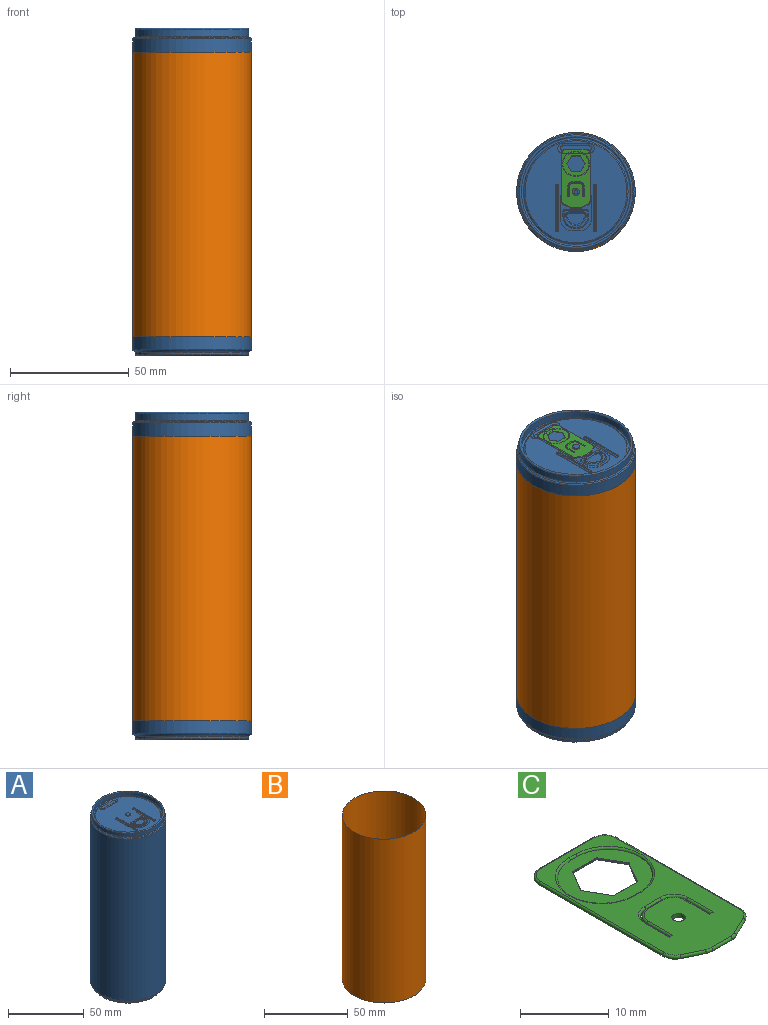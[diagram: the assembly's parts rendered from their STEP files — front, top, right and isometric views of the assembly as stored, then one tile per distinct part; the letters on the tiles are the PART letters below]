
ASSEMBLY  parts=3 mates=2
PART A: 76 faces, bbox 54.1x54.1x138 mm
  f0: plane 43x43mm, normal (0,0,1), area 1250.3mm2, adj f1,f7,f8,f9,f14,f18,f19,f20
  f1: plane 1x0.01mm, normal (0,-1,0), area 0mm2, adj f0,f9,f18
  f2: cylinder r=25mm len=131mm, axis (0,0,-1), area 20577.4mm2, adj f60,f66
  f3: cylinder r=24mm len=48mm, axis (0,0,1), area 150.8mm2, adj f67,f68
  f4: plane 43x43mm, normal (0,0,-1), area 1452.2mm2, adj f75
  f5: cylinder r=23mm len=46mm, axis (0,0,-1), area 433.5mm2, adj f59,f62
  f6: cylinder r=24mm len=48mm, axis (0,0,-1), area 452.4mm2, adj f61,f62
  f7: plane 3x1mm, normal (0,1,0), area 3mm2, adj f0,f10,f25,f26
  f8: plane 10.02x1.02mm, normal (-1,0,0), area 10mm2, adj f0,f10,f19,f25
  f9: plane 10x1mm, normal (1,0,0), area 10mm2, adj f0,f1,f10,f26
  f10: plane 41x41mm, normal (0,0,-1), area 1319.8mm2, adj f7,f8,f9,f18,f19,f20,f23,f24
  f11: plane 48x48mm, normal (0,0,1), area 1809.6mm2, adj f69
  f12: cylinder r=24.5mm len=129mm, axis (0,0,-1), area 19858mm2, adj f65,f69
  f13: plane 48x48mm, normal (0,0,-1), area 357.4mm2, adj f63,f65
  f14: cylinder r=0.75mm len=1.5mm, axis (0,0,-1), area 2.4mm2, adj f0,f17
  f15: cylinder r=1.5mm len=3mm, axis (0,0,-1), area 4.7mm2, adj f16,f17
  f16: plane 3x3mm, normal (0,0,1), area 7.1mm2, adj f15
  f17: plane 3x3mm, normal (0,0,-1), area 5.3mm2, adj f14,f15
  f18: plane 9.99x1mm, normal (-1,0,0), area 10mm2, adj f0,f1,f10,f23
  f19: plane 10.01x1.02mm, normal (1,0,0), area 10mm2, adj f0,f8,f10,f24
  f20: plane 2.98x1mm, normal (0,-1,0), area 3mm2, adj f0,f10,f23,f24
  f21: plane 9.98x6.99mm, normal (0,0,1), area 21.4mm2, adj f27,f28,f29,f30,f31,f32,f33,f34
  f22: plane 7.72x4.89mm, normal (0,0,1), area 28.5mm2, adj f35,f36,f37,f38,f39
  f23: cylinder r=5mm len=5mm, axis (0,0,1), area 7.9mm2, adj f0,f10,f18,f20
  f24: cylinder r=5mm len=5mm, axis (0,0,-1), area 7.9mm2, adj f0,f10,f19,f20
  f25: cylinder r=5mm len=5mm, axis (0,0,1), area 7.9mm2, adj f0,f7,f8,f10
  f26: cylinder r=5mm len=5mm, axis (0,0,-1), area 7.9mm2, adj f0,f7,f9,f10
  f27: torus R=4.5mm, axis (0,0,1), area 5.9mm2, adj f0,f21,f28,f29
  f28: cylinder r=0.5mm len=1.99mm, axis (0,-1,0), area 1.6mm2, adj f0,f21,f27,f30
  f29: cylinder r=0.5mm len=0.98mm, axis (-1,0,0), area 0.8mm2, adj f0,f21,f27,f31
  f30: torus R=0.5mm, axis (0,0,1), area 1mm2, adj f0,f21,f28,f32
  f31: torus R=4.5mm, axis (0,0,1), area 5.9mm2, adj f0,f21,f29,f33
  f32: cylinder r=0.5mm len=8.98mm, axis (1,0,0), area 7.1mm2, adj f0,f21,f30,f34
  f33: cylinder r=0.5mm len=1.99mm, axis (0,1,0), area 1.6mm2, adj f0,f21,f31,f34
  f34: torus R=0.5mm, axis (0,0,1), area 1mm2, adj f0,f21,f32,f33
  f35: torus R=1.5mm, axis (0,0,1), area 1.7mm2, adj f21,f22,f36,f37
  f36: torus R=5.5mm, axis (0,0,1), area 4.6mm2, adj f21,f22,f35,f38
  f37: cylinder r=0.5mm len=5.72mm, axis (-1,0,0), area 4.5mm2, adj f21,f22,f35,f39
  f38: torus R=5.5mm, axis (0,0,1), area 4.6mm2, adj f21,f22,f36,f39
  f39: torus R=1.5mm, axis (0,0,1), area 1.7mm2, adj f21,f22,f37,f38
  f40: plane 19x0.5mm, normal (0,0,1), area 9.5mm2, adj f43,f44,f47,f48
  f41: plane 19x0.5mm, normal (0,0,1), area 9.5mm2, adj f51,f52,f55,f56
  f42: sphere r=0.5mm, area 0.4mm2, adj f0,f43,f44
  f43: cylinder r=0.5mm len=19mm, axis (0,-1,0), area 14.9mm2, adj f0,f40,f42,f45
  f44: cylinder r=0.5mm len=0.5mm, axis (-1,0,0), area 0.4mm2, adj f0,f40,f42,f46
  f45: sphere r=0.5mm, area 0.2mm2, adj f0,f43,f47
  f46: sphere r=0.5mm, area 0.4mm2, adj f0,f44,f48
  f47: cylinder r=0.5mm len=0.5mm, axis (1,0,0), area 0.4mm2, adj f0,f40,f45,f49
  f48: cylinder r=0.5mm len=19mm, axis (0,1,0), area 14.9mm2, adj f0,f40,f46,f49
  f49: sphere r=0.5mm, area 0.4mm2, adj f0,f47,f48
  f50: sphere r=0.5mm, area 0.4mm2, adj f0,f51,f52
  f51: cylinder r=0.5mm len=0.5mm, axis (-1,0,0), area 0.4mm2, adj f0,f41,f50,f53
  f52: cylinder r=0.5mm len=19mm, axis (0,1,0), area 14.9mm2, adj f0,f41,f50,f54
  f53: sphere r=0.5mm, area 0.4mm2, adj f0,f51,f55
  f54: sphere r=0.5mm, area 0.4mm2, adj f0,f52,f56
  f55: cylinder r=0.5mm len=19mm, axis (0,-1,0), area 14.9mm2, adj f0,f41,f53,f57
  f56: cylinder r=0.5mm len=0.5mm, axis (1,0,0), area 0.4mm2, adj f0,f41,f54,f57
  f57: sphere r=0.5mm, area 0.2mm2, adj f0,f55,f56
  f58: torus R=21.5mm, axis (0,0,1), area 107.7mm2, adj f0,f59
  f59: torus R=22.5mm, axis (0,0,1), area 222.1mm2, adj f5,f58
  f60: torus R=24.5mm, axis (0,0,1), area 122.5mm2, adj f2,f61
  f61: torus R=24.5mm, axis (0,0,1), area 119.3mm2, adj f6,f60
  f62: torus R=23.5mm, axis (0,0,1), area 231.9mm2, adj f5,f6
  f63: torus R=21.5mm, axis (0,0,1), area 104.5mm2, adj f13,f64
  f64: torus R=20.5mm, axis (0,0,1), area 102.7mm2, adj f10,f63
  f65: torus R=24mm, axis (0,0,1), area 120mm2, adj f12,f13
  f66: torus R=24.5mm, axis (0,0,1), area 122.5mm2, adj f2,f67
  f67: torus R=24.5mm, axis (0,0,1), area 119.3mm2, adj f3,f66
  f68: torus R=23.5mm, axis (0,0,-1), area 231.9mm2, adj f3,f75
  f69: torus R=24mm, axis (0,0,1), area 120mm2, adj f11,f12
  f70: plane 12.99x2mm, normal (0,0,1), area 25.1mm2, adj f71,f72,f73,f74
  f71: cylinder r=3mm len=10.99mm, axis (1,0,0), area 13.6mm2, adj f0,f70,f72,f73
  f72: torus R=2.2mm, axis (0,0,1), area 6.2mm2, adj f0,f70,f71,f74
  f73: torus R=2.2mm, axis (0,0,1), area 6.2mm2, adj f0,f70,f71,f74
  f74: cylinder r=3mm len=10.99mm, axis (1,0,0), area 13.6mm2, adj f0,f70,f72,f73
  f75: torus R=21.5mm, axis (0,0,1), area 332.4mm2, adj f4,f68
PART B: 4 faces, bbox 50x50x120 mm
  f0: cylinder r=25mm len=120mm, axis (0,0,-1), area 18849.6mm2, adj f2,f3
  f1: cylinder r=25.01mm len=120mm, axis (0,0,-1), area 18857.1mm2, adj f2,f3
  f2: plane 50.02x50.02mm, normal (0,0,1), area 1.6mm2, adj f0,f1
  f3: plane 50.02x50.02mm, normal (0,0,-1), area 1.6mm2, adj f0,f1
PART C: 50 faces, bbox 12.8x25.3x0.5 mm
  f0: plane 11x10mm, normal (0,0,1), area 50.3mm2, adj f18,f19,f20,f21,f22,f23,f46,f47
  f1: plane 24.5x12mm, normal (0,0,-1), area 234.1mm2, adj f3,f4,f5,f12,f13,f14,f15,f16
  f2: plane 24.5x12mm, normal (0,0,1), area 175.2mm2, adj f3,f4,f5,f24,f25,f26,f27,f28
  f3: plane 0.6x0.5mm, normal (0,1,0), area 0.1mm2, adj f1,f2,f36,f41
  f4: plane 0.6x0.5mm, normal (0,1,0), area 0.1mm2, adj f1,f2,f40,f45
  f5: cylinder r=0.76mm len=1.51mm, axis (0,0,1), area 2.4mm2, adj f1,f2
  f6: plane 3.27x1.89mm, normal (0.87,-0.5,0), area 0.6mm2, adj f7,f11,f17,f19
  f7: plane 3.27x1.89mm, normal (0.87,0.5,0), area 0.6mm2, adj f6,f8,f15,f18
  f8: plane 3.78x0.15mm, normal (0,1,0), area 0.6mm2, adj f7,f9,f13,f20
  f9: plane 3.27x1.89mm, normal (-0.87,0.5,0), area 0.6mm2, adj f8,f10,f12,f22
  f10: plane 3.27x1.89mm, normal (-0.87,-0.5,0), area 0.6mm2, adj f9,f11,f14,f23
  f11: plane 3.78x0.15mm, normal (0,-1,0), area 0.6mm2, adj f6,f10,f16,f21
  f12: cylinder r=0.05mm len=3.35mm, axis (0.5,0.87,0), area 0.3mm2, adj f1,f9,f13,f14
  f13: cylinder r=0.05mm len=3.84mm, axis (1,0,0), area 0.3mm2, adj f1,f8,f12,f15
  f14: cylinder r=0.05mm len=3.35mm, axis (-0.5,0.87,0), area 0.3mm2, adj f1,f10,f12,f16
  f15: cylinder r=0.05mm len=3.35mm, axis (0.5,-0.87,0), area 0.3mm2, adj f1,f7,f13,f17
  f16: cylinder r=0.05mm len=3.84mm, axis (-1,0,0), area 0.3mm2, adj f1,f11,f14,f17
  f17: cylinder r=0.05mm len=3.35mm, axis (-0.5,-0.87,0), area 0.3mm2, adj f1,f6,f15,f16
  f18: cylinder r=0.05mm len=3.35mm, axis (-0.5,0.87,0), area 0.3mm2, adj f0,f7,f19,f20
  f19: cylinder r=0.05mm len=3.35mm, axis (0.5,0.87,0), area 0.3mm2, adj f0,f6,f18,f21
  f20: cylinder r=0.05mm len=3.84mm, axis (-1,0,0), area 0.3mm2, adj f0,f8,f18,f22
  f21: cylinder r=0.05mm len=3.84mm, axis (1,0,0), area 0.3mm2, adj f0,f11,f19,f23
  f22: cylinder r=0.05mm len=3.35mm, axis (-0.5,-0.87,0), area 0.3mm2, adj f0,f9,f20,f23
  f23: cylinder r=0.05mm len=3.35mm, axis (0.5,-0.87,0), area 0.3mm2, adj f0,f10,f21,f22
  f24: cylinder r=0.25mm len=2.82mm, axis (0.9,-0.44,0), area 2.4mm2, adj f1,f2,f25,f26
  f25: torus R=1.75mm, axis (0,0,1), area 1.7mm2, adj f1,f2,f24,f27
  f26: torus R=1.75mm, axis (0,0,1), area 0.7mm2, adj f1,f2,f24,f28
  f27: cylinder r=0.25mm len=19.68mm, axis (0,1,0), area 15.5mm2, adj f1,f2,f25,f29
  f28: cylinder r=0.25mm len=3.08mm, axis (-1,0,0), area 2.4mm2, adj f1,f2,f26,f30
  f29: torus R=1.75mm, axis (0,0,1), area 2.4mm2, adj f1,f2,f27,f31
  f30: torus R=1.75mm, axis (0,0,1), area 0.7mm2, adj f1,f2,f28,f32
  f31: cylinder r=0.25mm len=8.5mm, axis (1,0,0), area 6.7mm2, adj f1,f2,f29,f33
  f32: cylinder r=0.25mm len=2.82mm, axis (0.9,0.44,0), area 2.4mm2, adj f1,f2,f30,f34
  f33: torus R=1.75mm, axis (0,0,1), area 2.4mm2, adj f1,f2,f31,f35
  f34: torus R=1.75mm, axis (0,0,1), area 1.7mm2, adj f1,f2,f32,f35
  f35: cylinder r=0.25mm len=19.68mm, axis (0,-1,0), area 15.5mm2, adj f1,f2,f33,f34
  f36: cylinder r=0.25mm len=4mm, axis (0,-1,0), area 3.1mm2, adj f1,f2,f3,f37
  f37: torus R=2.25mm, axis (0,0,1), area 2.6mm2, adj f1,f2,f36,f38
  f38: cylinder r=0.25mm len=2.5mm, axis (1,0,0), area 2mm2, adj f1,f2,f37,f39
  f39: torus R=2.25mm, axis (0,0,1), area 2.6mm2, adj f1,f2,f38,f40
  f40: cylinder r=0.25mm len=4mm, axis (0,1,0), area 3.1mm2, adj f1,f2,f4,f39
  f41: cylinder r=0.25mm len=3.9mm, axis (0,-1,0), area 3.1mm2, adj f1,f2,f3,f42
  f42: torus R=1.75mm, axis (0,0,1), area 2.4mm2, adj f1,f2,f41,f43
  f43: cylinder r=0.25mm len=2.3mm, axis (-1,0,0), area 1.8mm2, adj f1,f2,f42,f44
  f44: torus R=1.75mm, axis (0,0,1), area 2.4mm2, adj f1,f2,f43,f45
  f45: cylinder r=0.25mm len=3.9mm, axis (0,1,0), area 3.1mm2, adj f1,f2,f4,f44
  f46: torus R=5.25mm, axis (0,0,1), area 6.3mm2, adj f0,f2,f47,f48
  f47: cylinder r=0.25mm len=1mm, axis (1,0,0), area 0.4mm2, adj f0,f2,f46,f49
  f48: cylinder r=0.25mm len=1mm, axis (-1,0,0), area 0.4mm2, adj f0,f2,f46,f49
  f49: torus R=5.25mm, axis (0,0,1), area 6.3mm2, adj f0,f2,f47,f48
PLACE A t=(-15.61,-10.39,-2.32)mm fixed
PLACE B t=(-15.61,-10.39,3.68)mm
PLACE C t=(-15.61,-4.89,130.69)mm
MATE fastened B.f1 <-> A.f2  axis (0,0,-1) through (-15.61,-10.39,63.68)mm
MATE cylindrical C.f5 <-> A.f15  axis (0,0,1) through (-15.61,-10.39,131.19)mm
